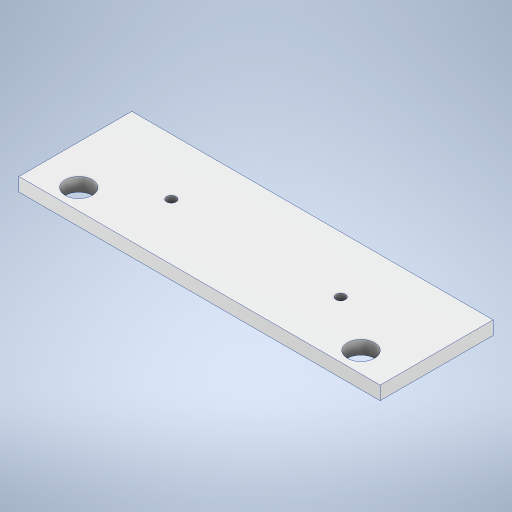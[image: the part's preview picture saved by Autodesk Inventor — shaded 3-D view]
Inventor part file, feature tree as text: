
AUTODESK INVENTOR PART (.ipt)
format: ipt  version: 2023.2 (Build 272271000, 271)  size: 246,272 bytes
history: native  units: mm
features: sketch x2, extrude x1, hole x1
ambient origin geometry x8: Origin, YZ Plane, XZ Plane, XY Plane, X Axis, Y Axis, Z Axis, Center Point
bodies: Solid1 (feature_tree)
feature tree (4):
  extrude  "Extrusion1"  Depth=50.0mm
  hole  "Hole1"  [1 undecoded]
  sketch  "Sketch1"  dims[d0=160.0mm d1=50.0mm]
  sketch  "Sketch2"  dims[d2=9.0mm d3=12.0mm d4=12.0mm d5=125.0mm d6=17.5mm d7=6.0mm d8=0.0mm d9=4.8mm d10=4.8mm d11=75.0mm d12=42.5mm d13=4.134mm d14=10.0mm d15=4.0mm d16=2.0mm d17=90.0deg d18=8.0mm d19=20.594885mm]
note: 1 required parameter value undecoded (feature->parameter linkage not recoverable at this tier; creation-order binding heuristic only, values carry confidence <= 0.55)
